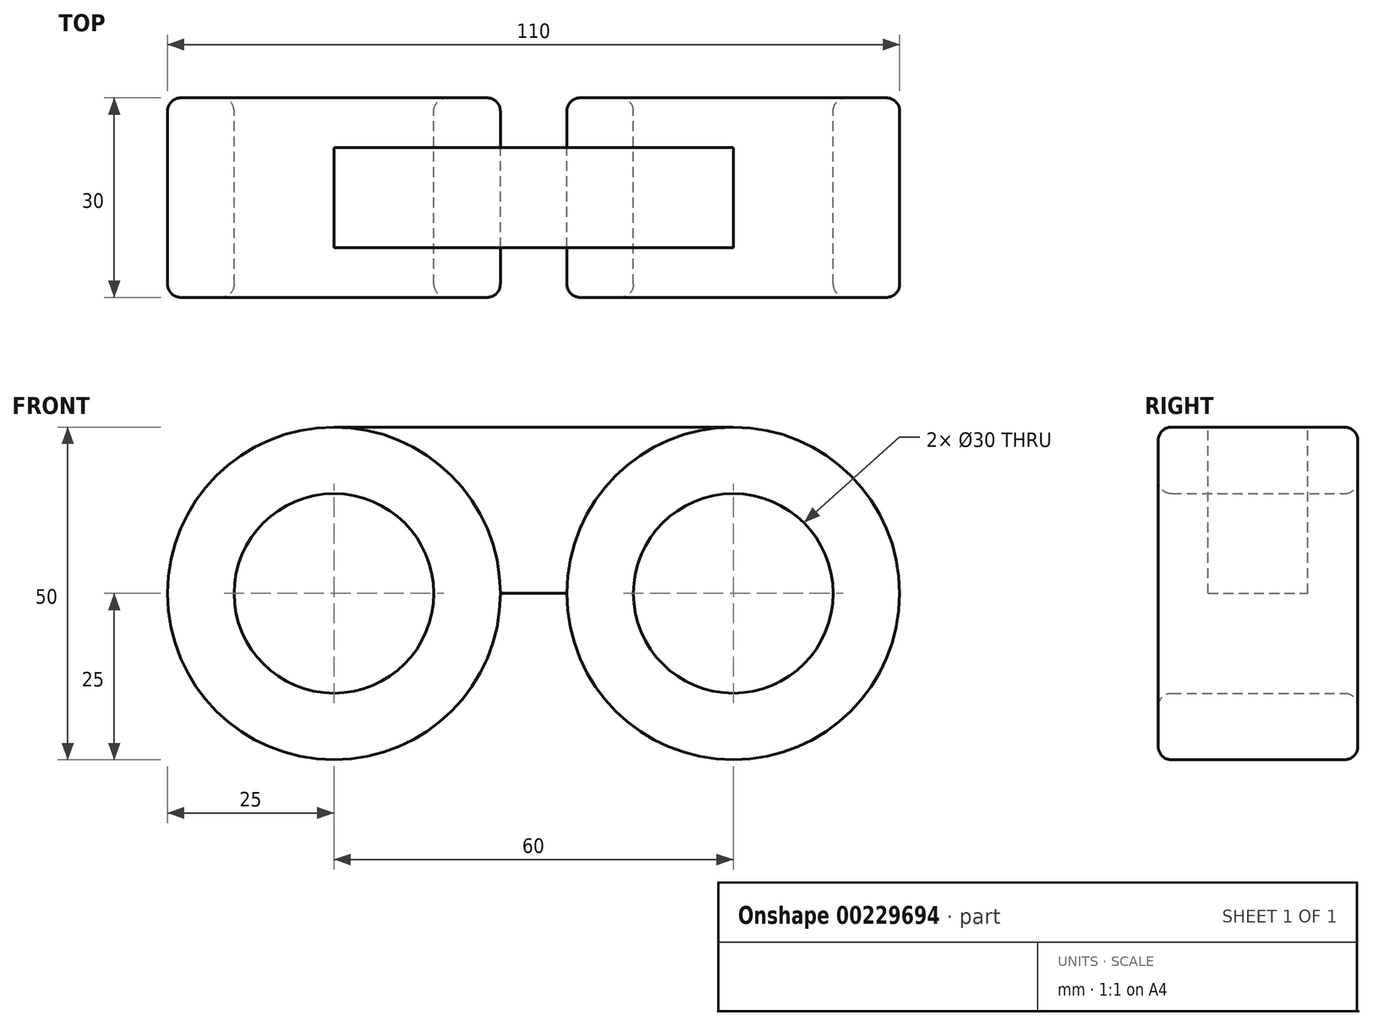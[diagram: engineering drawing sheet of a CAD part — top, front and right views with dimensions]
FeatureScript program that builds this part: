
annotation { "Feature Type Name" : "Feature", "Feature Type Description" : "" }
export const myFeature = defineFeature(function(context is Context, id is Id, definition is map)
    precondition{}
    {
        {
            var Q0;
            Q0=qCreatedBy(makeId("Front.planeOp"),FACE);
            var sketch = newSketch(context, id + "F0", { "sketchPlane" : qUnion([Q0])});
            skCircle(sketch, "E0", {"center": v(0, 0) * mm, "radius": 25 * mm});
            skCircle(sketch, "E1", {"center": v(0, 0) * mm, "radius": 15 * mm});
            skCircle(sketch, "E2", {"center": v(60, 0) * mm, "radius": 25 * mm});
            skLineSegment(sketch, "E3.bottom", {"start": v(0, 0) * mm, "end": v(15, 0) * mm});
            skLineSegment(sketch, "E3.top", {"start": v(0, 25) * mm, "end": v(60, 25) * mm});
            skLineSegment(sketch, "E3.left", {"start": v(0, 0) * mm, "end": v(0, 15) * mm});
            skLineSegment(sketch, "E3.right", {"start": v(60, 0) * mm, "end": v(60, 25) * mm});
            skLineSegment(sketch, "E4", {"start": v(0, 15) * mm, "end": v(0, 25) * mm});
            skLineSegment(sketch, "E5", {"start": v(15, 0) * mm, "end": v(60, 0) * mm});
            skArc(sketch, "E6", {"start": v(60, 15) * mm, "mid": v(49.4, 10.6) * mm, "end": v(45, 0) * mm});
            skLineSegment(sketch, "E7", {"start": v(45, 0) * mm, "end": v(45, 0) * mm});
            skArc(sketch, "E8", {"start": v(45, 0) * mm, "mid": v(70.6, -10.6) * mm, "end": v(60, 15) * mm});
            skLineSegment(sketch, "E9", {"start": v(15, 0) * mm, "end": v(15, 0) * mm});
            skSolve(sketch);
        }
        {
            var Q0;
            {var subQ0=sQuery(id+"F0.wireOp",EDGE,"E4");Q0=makeQuery(id+"F0.imprint","IMPRINT",FACE,{"disambiguationData":[TD([[makeQuery(id+"F0.imprint","IMPRINT",EDGE,{"derivedFrom":subQ0}),1.0]])]});}
            var Q1;
            {var subQ0=sQuery(id+"F0.wireOp",EDGE,"E4");Q1=makeQuery(id+"F0.imprint","IMPRINT",FACE,{"disambiguationData":[TD([[makeQuery(id+"F0.imprint","IMPRINT",EDGE,{"derivedFrom":subQ0}),-1.0]])]});}
            var Q2;
            {var subQ5=sQuery(id+"F0.wireOp",EDGE,"E8");Q2=makeQuery(id+"F0.imprint","IMPRINT",FACE,{"disambiguationData":[TD([[makeQuery(id+"F0.imprint","IMPRINT",EDGE,{"derivedFrom":subQ5}),-1.0]])]});}
            var Q3;
            {var subQ6=sQuery(id+"F0.wireOp",EDGE,"E6");Q3=makeQuery(id+"F0.imprint","IMPRINT",FACE,{"disambiguationData":[TD([[makeQuery(id+"F0.imprint","IMPRINT",EDGE,{"derivedFrom":subQ6}),-1.0]])]});}
            extrude(context, id + "F1", {"entities" : qUnion([Q0, Q1, Q2, Q3]), "endBound" : BoundingType.SYMMETRIC, "depth" : 30 * mm, "hasSecondDirection" : true, "secondDirectionOppositeDirection" : true, "secondDirectionDepth" : 25 * mm});
        }
        {
            var Q0;
            {var subQ0=sQuery(id+"F0.wireOp",EDGE,"E3.top");Q0=makeQuery(id+"F0.imprint","IMPRINT",FACE,{"disambiguationData":[TD([[makeQuery(id+"F0.imprint","IMPRINT",EDGE,{"derivedFrom":subQ0}),-1.0]])]});}
            extrude(context, id + "F2", {"entities" : qUnion([Q0]), "endBound" : BoundingType.SYMMETRIC, "depth" : 15 * mm});
        }
        {
            var Q0;
            Q0=makeQuery(id+"F1.opExtrude","CAP_FACE",FACE,{"disambiguationData":[OSD([sQuery(id+"F0.wireOp",EDGE,"E2"),sQuery(id+"F0.wireOp",EDGE,"E6"),sQuery(id+"F0.wireOp",EDGE,"E8")])],"isStart":true});
            var Q1;
            Q1=makeQuery(id+"F1.opExtrude","CAP_FACE",FACE,{"disambiguationData":[OSD([sQuery(id+"F0.wireOp",EDGE,"E0"),sQuery(id+"F0.wireOp",EDGE,"E1")])],"isStart":true});
            var Q2;
            Q2=makeQuery(id+"F1.opExtrude","CAP_FACE",FACE,{"disambiguationData":[OSD([sQuery(id+"F0.wireOp",EDGE,"E0"),sQuery(id+"F0.wireOp",EDGE,"E1")])],"isStart":false});
            var Q3;
            Q3=makeQuery(id+"F1.opExtrude","CAP_FACE",FACE,{"disambiguationData":[OSD([sQuery(id+"F0.wireOp",EDGE,"E2"),sQuery(id+"F0.wireOp",EDGE,"E6"),sQuery(id+"F0.wireOp",EDGE,"E8")])],"isStart":false});
            fillet(context, id + "F3", {"entities" : qUnion([Q0, Q1, Q2, Q3]), "radius" : 2 * mm, "tangentPropagation" : true, "allowEdgeOverflow" : false});
        }
    });
